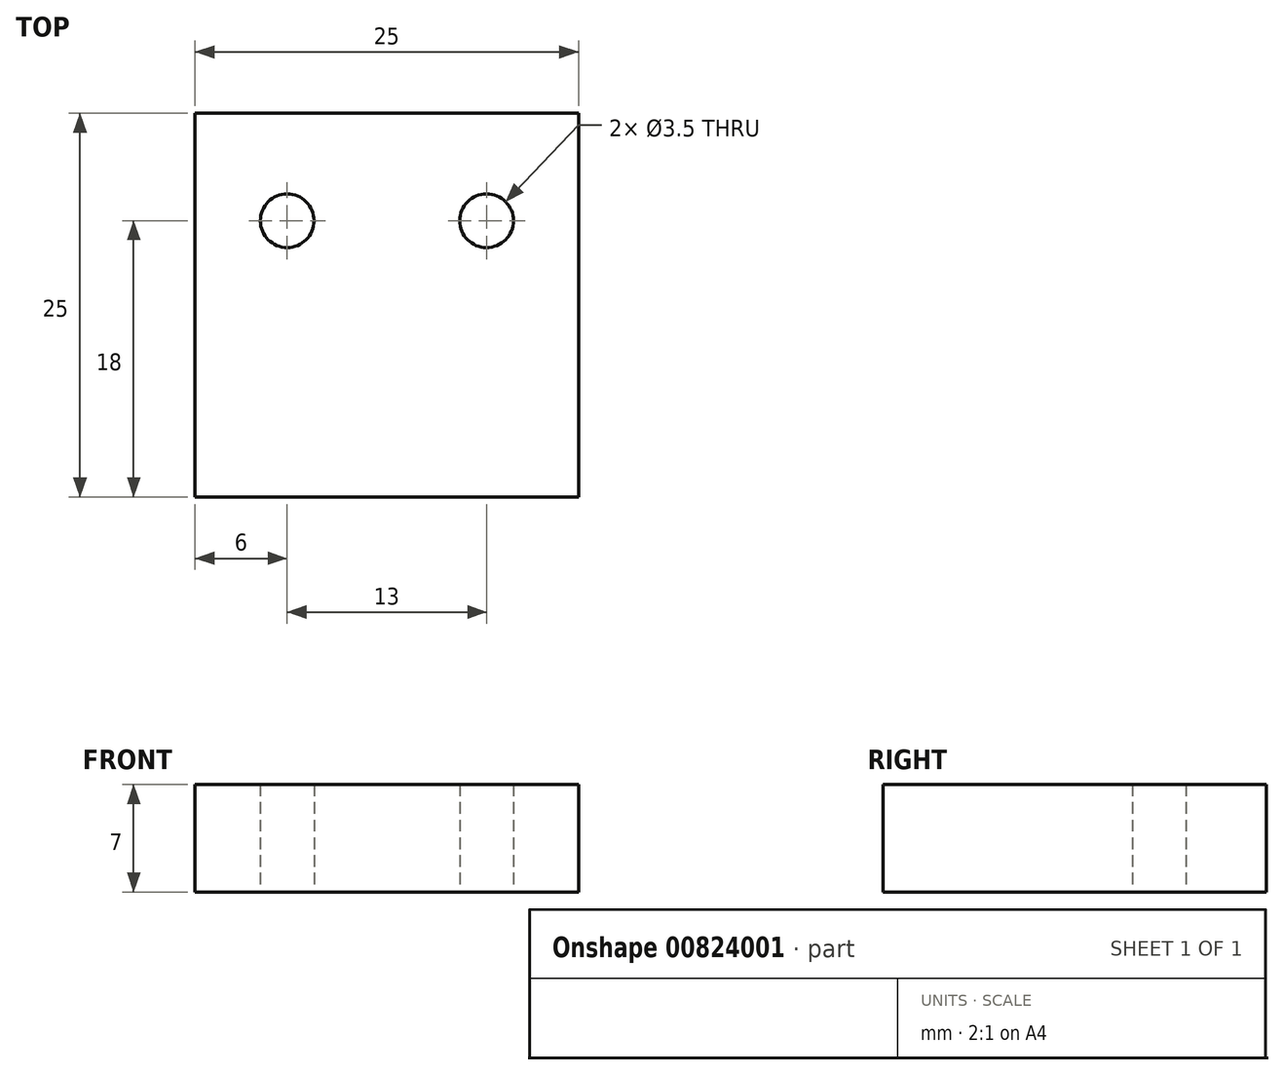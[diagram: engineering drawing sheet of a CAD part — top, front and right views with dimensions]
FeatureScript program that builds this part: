
annotation { "Feature Type Name" : "Feature", "Feature Type Description" : "" }
export const myFeature = defineFeature(function(context is Context, id is Id, definition is map)
    precondition{}
    {
        {
            var Q0;
            Q0=qCreatedBy(makeId("Top.planeOp"),FACE);
            var sketch = newSketch(context, id + "F0", { "sketchPlane" : qUnion([Q0])});
            skLineSegment(sketch, "E0.bottom", {"start": v(0, 0) * mm, "end": v(25, 0) * mm});
            skLineSegment(sketch, "E0.top", {"start": v(0, 25) * mm, "end": v(25, 25) * mm});
            skLineSegment(sketch, "E0.left", {"start": v(0, 0) * mm, "end": v(0, 25) * mm});
            skLineSegment(sketch, "E0.right", {"start": v(25, 0) * mm, "end": v(25, 25) * mm});
            skCircle(sketch, "E1", {"center": v(6, 18) * mm, "radius": 1.75 * mm});
            skCircle(sketch, "E2", {"center": v(19, 18) * mm, "radius": 1.75 * mm});
            skSolve(sketch);
        }
        {
            var Q0;
            Q0 = qSketchRegion(id + "F0", true);
            extrude(context, id + "F1", {"entities" : qUnion([Q0]), "depth" : 7 * mm, "offsetDistance" : 25 * mm});
        }
    });
